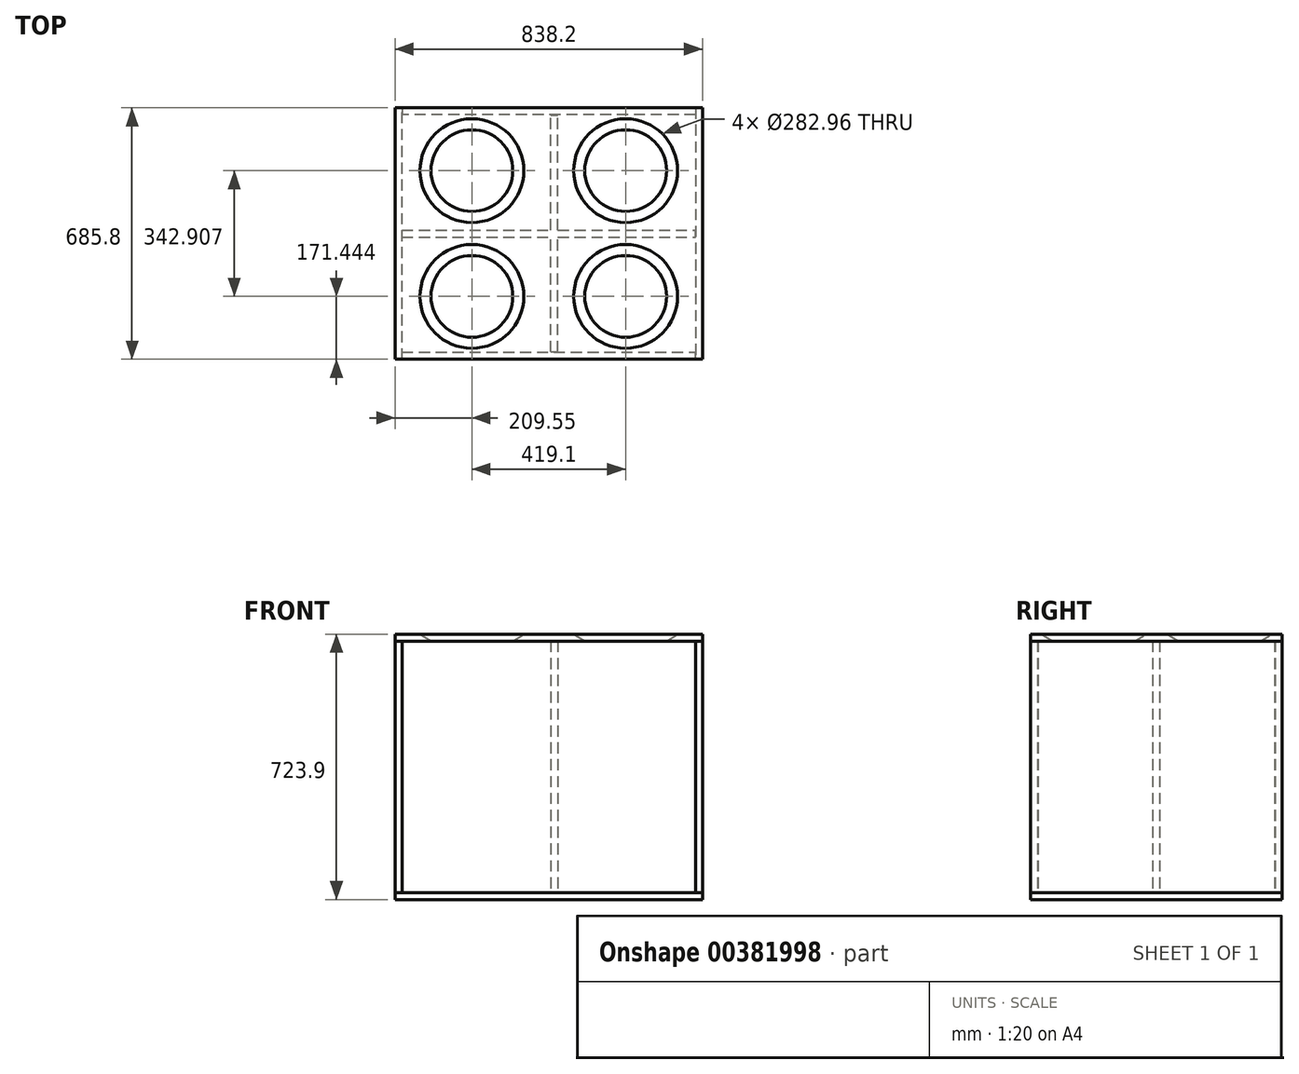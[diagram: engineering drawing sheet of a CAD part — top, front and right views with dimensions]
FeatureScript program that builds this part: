
annotation { "Feature Type Name" : "Feature", "Feature Type Description" : "" }
export const myFeature = defineFeature(function(context is Context, id is Id, definition is map)
    precondition{}
    {
        {
            var Q0;
            Q0=qCreatedBy(makeId("Top.planeOp"),FACE);
            var sketch = newSketch(context, id + "F0", { "sketchPlane" : qUnion([Q0])});
            skLineSegment(sketch, "E0.bottom", {"start": v(0, 685.8) * mm, "end": v(838.2, 685.8) * mm});
            skLineSegment(sketch, "E0.top", {"start": v(0, 0) * mm, "end": v(838.2, 0) * mm});
            skLineSegment(sketch, "E0.left", {"start": v(0, 685.8) * mm, "end": v(0, 0) * mm});
            skLineSegment(sketch, "E0.right", {"start": v(838.2, 685.8) * mm, "end": v(838.2, 0) * mm});
            skSolve(sketch);
        }
        {
            var Q0;
            Q0=makeQuery(id+"F0.imprint","IMPRINT",FACE,{"disambiguationData":[TD([[makeQuery(id+"F0.imprint","IMPRINT",EDGE,{"derivedFrom":sQuery(id+"F0.wireOp",EDGE,"E0.bottom")}),-1.0]])]});
            extrude(context, id + "F1", {"entities" : qUnion([Q0]), "depth" : 19.05 * mm});
        }
        {
            var Q0;
            Q0=makeQuery(id+"F1.opExtrude","CAP_FACE",FACE,{"disambiguationData":[OSD([sQuery(id+"F0.wireOp",EDGE,"E0.bottom"),sQuery(id+"F0.wireOp",EDGE,"E0.top"),sQuery(id+"F0.wireOp",EDGE,"E0.left"),sQuery(id+"F0.wireOp",EDGE,"E0.right")])],"isStart":false});
            var sketch = newSketch(context, id + "F2", { "sketchPlane" : qUnion([Q0])});
            skLineSegment(sketch, "E1.bottom", {"start": v(838.2, 685.8) * mm, "end": v(819.15, 685.8) * mm});
            skLineSegment(sketch, "E1.top", {"start": v(838.2, 0) * mm, "end": v(819.15, 0) * mm});
            skLineSegment(sketch, "E1.left", {"start": v(838.2, 685.8) * mm, "end": v(838.2, 0) * mm});
            skLineSegment(sketch, "E1.right", {"start": v(819.15, 685.8) * mm, "end": v(819.15, 0) * mm});
            skLineSegment(sketch, "E2.bottom", {"start": v(0, 0) * mm, "end": v(19.05, 0) * mm});
            skLineSegment(sketch, "E2.top", {"start": v(0, 685.8) * mm, "end": v(19.05, 685.8) * mm});
            skLineSegment(sketch, "E2.left", {"start": v(0, 0) * mm, "end": v(0, 685.8) * mm});
            skLineSegment(sketch, "E2.right", {"start": v(19.05, 0) * mm, "end": v(19.05, 685.8) * mm});
            skSolve(sketch);
        }
        {
            var Q0;
            Q0 = qSketchRegion(id + "F2", true);
            extrude(context, id + "F3", {"entities" : qUnion([Q0]), "depth" : 685.8 * mm});
        }
        {
            var Q0;
            Q0=makeQuery(id+"F1.opExtrude","CAP_FACE",FACE,{"disambiguationData":[OSD([sQuery(id+"F0.wireOp",EDGE,"E0.bottom"),sQuery(id+"F0.wireOp",EDGE,"E0.top"),sQuery(id+"F0.wireOp",EDGE,"E0.left"),sQuery(id+"F0.wireOp",EDGE,"E0.right")])],"isStart":false});
            var sketch = newSketch(context, id + "F4", { "sketchPlane" : qUnion([Q0])});
            skLineSegment(sketch, "E3.bottom", {"start": v(819.15, 685.8) * mm, "end": v(19.05, 685.8) * mm});
            skLineSegment(sketch, "E3.top", {"start": v(819.15, 666.75) * mm, "end": v(19.05, 666.75) * mm});
            skLineSegment(sketch, "E3.left", {"start": v(819.15, 685.8) * mm, "end": v(819.15, 666.75) * mm});
            skLineSegment(sketch, "E3.right", {"start": v(19.05, 685.8) * mm, "end": v(19.05, 666.75) * mm});
            skLineSegment(sketch, "E4.bottom", {"start": v(19.05, 0) * mm, "end": v(819.15, 0) * mm});
            skLineSegment(sketch, "E4.top", {"start": v(19.05, 19.05) * mm, "end": v(819.15, 19.05) * mm});
            skLineSegment(sketch, "E4.left", {"start": v(19.05, 0) * mm, "end": v(19.05, 19.05) * mm});
            skLineSegment(sketch, "E4.right", {"start": v(819.15, 0) * mm, "end": v(819.15, 19.05) * mm});
            skSolve(sketch);
        }
        {
            var Q0;
            Q0 = qSketchRegion(id + "F4", true);
            extrude(context, id + "F5", {"entities" : qUnion([Q0]), "depth" : 685.8 * mm});
        }
        {
            var Q0;
            Q0=makeQuery(id+"F1.opExtrude","CAP_FACE",FACE,{"disambiguationData":[OSD([sQuery(id+"F0.wireOp",EDGE,"E0.bottom"),sQuery(id+"F0.wireOp",EDGE,"E0.top"),sQuery(id+"F0.wireOp",EDGE,"E0.left"),sQuery(id+"F0.wireOp",EDGE,"E0.right")])],"isStart":false});
            var sketch = newSketch(context, id + "F6", { "sketchPlane" : qUnion([Q0])});
            skLineSegment(sketch, "E5.bottom", {"start": v(424.78, 20.11) * mm, "end": v(443.83, 20.11) * mm});
            skLineSegment(sketch, "E5.top", {"start": v(424.78, 665.27) * mm, "end": v(443.83, 665.27) * mm});
            skLineSegment(sketch, "E5.left", {"start": v(424.78, 20.11) * mm, "end": v(424.78, 665.27) * mm});
            skLineSegment(sketch, "E5.right", {"start": v(443.83, 20.11) * mm, "end": v(443.83, 665.27) * mm});
            skLineSegment(sketch, "E6.bottom", {"start": v(19.05, 333.17) * mm, "end": v(819.15, 333.17) * mm});
            skLineSegment(sketch, "E6.top", {"start": v(19.05, 352.22) * mm, "end": v(819.15, 352.22) * mm});
            skLineSegment(sketch, "E6.left", {"start": v(19.05, 333.17) * mm, "end": v(19.05, 352.22) * mm});
            skLineSegment(sketch, "E6.right", {"start": v(819.15, 333.17) * mm, "end": v(819.15, 352.22) * mm});
            skLineSegment(sketch, "E7.bottom", {"start": v(52.97, 352.22) * mm, "end": v(819.15, 352.22) * mm});
            skLineSegment(sketch, "E7.top", {"start": v(52.97, 333.17) * mm, "end": v(819.15, 333.17) * mm});
            skLineSegment(sketch, "E7.left", {"start": v(52.97, 352.22) * mm, "end": v(52.97, 333.17) * mm});
            skLineSegment(sketch, "E7.right", {"start": v(819.15, 352.22) * mm, "end": v(819.15, 333.17) * mm});
            skSolve(sketch);
        }
        {
            var Q0;
            Q0=makeQuery(id+"F3.opExtrude","CAP_FACE",FACE,{"disambiguationData":[OSD([sQuery(id+"F2.wireOp",EDGE,"E2.bottom"),sQuery(id+"F2.wireOp",EDGE,"E2.top"),sQuery(id+"F2.wireOp",EDGE,"E2.left"),sQuery(id+"F2.wireOp",EDGE,"E2.right")])],"isStart":false});
            var sketch = newSketch(context, id + "F7", { "sketchPlane" : qUnion([Q0])});
            skLineSegment(sketch, "E8.bottom", {"start": v(0, 685.8) * mm, "end": v(838.2, 685.8) * mm});
            skLineSegment(sketch, "E8.top", {"start": v(0, 0) * mm, "end": v(838.2, 0) * mm});
            skLineSegment(sketch, "E8.left", {"start": v(0, 685.8) * mm, "end": v(0, 0) * mm});
            skLineSegment(sketch, "E8.right", {"start": v(838.2, 685.8) * mm, "end": v(838.2, 0) * mm});
            skSolve(sketch);
        }
        {
            var Q0;
            Q0 = qSketchRegion(id + "F7", true);
            extrude(context, id + "F8", {"entities" : qUnion([Q0]), "depth" : 19.05 * mm});
        }
        {
            var Q0;
            Q0=makeQuery(id+"F8.opExtrude","CAP_FACE",FACE,{"disambiguationData":[OSD([sQuery(id+"F7.wireOp",EDGE,"E8.bottom"),sQuery(id+"F7.wireOp",EDGE,"E8.top"),sQuery(id+"F7.wireOp",EDGE,"E8.left"),sQuery(id+"F7.wireOp",EDGE,"E8.right")])],"isStart":false});
            var sketch = newSketch(context, id + "F9", { "sketchPlane" : qUnion([Q0])});
            skLineSegment(sketch, "E9", {"start": v(419.1, 685.8) * mm, "end": v(419.1, 0) * mm});
            skLineSegment(sketch, "E10", {"start": v(0, 342.9) * mm, "end": v(838.2, 342.9) * mm});
            skLineSegment(sketch, "E11", {"start": v(0, 342.9) * mm, "end": v(0, 685.8) * mm});
            skLineSegment(sketch, "E12", {"start": v(0, 685.8) * mm, "end": v(419.1, 685.8) * mm});
            skLineSegment(sketch, "E13", {"start": v(838.2, 685.8) * mm, "end": v(838.2, 342.9) * mm});
            skLineSegment(sketch, "E14", {"start": v(419.1, 685.8) * mm, "end": v(838.2, 685.8) * mm});
            skLineSegment(sketch, "E15", {"start": v(0, 0) * mm, "end": v(0, 342.9) * mm});
            skLineSegment(sketch, "E16", {"start": v(0, 0) * mm, "end": v(419.1, 0) * mm});
            skLineSegment(sketch, "E17", {"start": v(419.1, 0) * mm, "end": v(838.2, 0) * mm});
            skLineSegment(sketch, "E18", {"start": v(838.2, 0) * mm, "end": v(838.2, 342.9) * mm});
            skPoint(sketch, "E19", {"position": v(209.55, 685.8) * mm});
            skPoint(sketch, "E20", {"position": v(0, 514.35) * mm});
            skCircle(sketch, "E21", {"center": v(209.55, 514.35) * mm, "radius": 141.48 * mm});
            skPoint(sketch, "E22", {"position": v(0, 171.45) * mm});
            skPoint(sketch, "E23", {"position": v(209.55, 0) * mm});
            skPoint(sketch, "E24", {"position": v(209.55, 171.44) * mm});
            skCircle(sketch, "E25", {"center": v(209.55, 171.44) * mm, "radius": 141.48 * mm});
            skPoint(sketch, "E26", {"position": v(628.65, 0) * mm});
            skCircle(sketch, "E27", {"center": v(628.65, 171.44) * mm, "radius": 141.48 * mm});
            skCircle(sketch, "E28", {"center": v(628.65, 514.35) * mm, "radius": 141.48 * mm});
            skPoint(sketch, "E28.centerSnap0", {"position": v(628.65, 685.8) * mm});
            skSolve(sketch);
        }
        {
            var Q0;
            Q0=sQuery(id+"F9.wireOp",VERTEX,"E21.center");
            var Q1;
            Q1=sQuery(id+"F9.wireOp",VERTEX,"E28.center");
            var Q2;
            Q2=sQuery(id+"F9.wireOp",VERTEX,"E27.center");
            var Q3;
            Q3=sQuery(id+"F9.wireOp",VERTEX,"E24");
            var Q4;
            Q4=makeQuery(id+"F8.opExtrude","SWEPT_BODY",BODY,{"disambiguationData":[OSD([sQuery(id+"F7.wireOp",EDGE,"E8.bottom"),sQuery(id+"F7.wireOp",EDGE,"E8.top"),sQuery(id+"F7.wireOp",EDGE,"E8.left"),sQuery(id+"F7.wireOp",EDGE,"E8.right")])]});
            hole(context, id + "F10", {"style" : HoleStyle.SIMPLE, "endStyle" : HoleEndStyle.BLIND, "holeDiameter" : 282.96 * mm, "holeDepth" : mm, "isTappedThrough" : true, "tappedDepth" : 12.7 * mm, "tapClearance" : 3, "startFromSketch" : true, "locations" : qUnion([Q0, Q1, Q2, Q3]), "scope" : qUnion([Q4])});
        }
        {
            var Q0;
            Q0 = qSketchRegion(id + "F6", true);
            extrude(context, id + "F11", {"entities" : qUnion([Q0]), "depth" : 685.8 * mm});
        }
    });
